# Revit family: Furniture_Table_Spacestor_Circa Boardroom Table
name_source: partatom
category: Furniture
revit_build: Autodesk Revit 2017 (Build: 20160225_1515(x64)
units: mm (PartAtom-declared; Revit-internal decimal feet)

## family parameters
Always vertical = Yes
Cut with Voids When Loaded = No
OmniClass Number = 23.40.20.00
OmniClass Title = General Furniture and Specialties
Room Calculation Point = No
Shared = No
Work Plane-Based = No

## types (23) — shared parameters
Assembly Code = E2020200
Fabric Finish = <By Category>
Legs Finish = <By Category>
Manufacturer = Spacestor
Table Top Finish = Spacestor White
URL = http://spacestor.uk.com

## per-type parameters (varying)
| type | Boat | Circular | Depth | Double D End | Oval | Rectangular | Width |
| boat-shaped - 2000w x 1000_800d x 727h | Yes | No | 1000 mm  [stored 3.28084 ft] | No | No | No | 2000 mm  [stored 6.56168 ft] |
| oval-shaped - 2000w x 1000d x 727h | No | No | 1000 mm  [stored 3.28084 ft] | No | Yes | No | 2000 mm  [stored 6.56168 ft] |
| double d-ended - 2000w x 1000d x 727h | No | No | 1000 mm  [stored 3.28084 ft] | Yes | No | No | 2000 mm  [stored 6.56168 ft] |
| circular - 1000 DIA x 727h | No | Yes | 1000 mm  [stored 3.28084 ft] | No | No | No | 3000 mm  [stored 9.84252 ft] |
| boat-shaped - 2400w x 1200_1000d x 727h | Yes | No | 1000 mm  [stored 3.28084 ft] | No | No | No | 2400 mm  [stored 7.87402 ft] |
| boat-shaped - 3000w x 1200_1000d x 727h | Yes | No | 1200 mm | No | No | No | 3000 mm  [stored 9.84252 ft] |
| boat-shaped - 3600w x 1200_1000d x 727h | Yes | No | 1200 mm | No | No | No | 3600 mm  [stored 11.811 ft] |
| boat-shaped - 4800w x 1200_1000d x 727h | Yes | No | 1200 mm | No | No | No | 4800 mm |
| circular - 1200 DIA x 727h | No | Yes | 1200 mm | No | No | No | 3000 mm  [stored 9.84252 ft] |
| circular - 800 DIA x 727h | No | Yes | 800 mm  [stored 2.62467 ft] | No | No | No | 3000 mm  [stored 9.84252 ft] |
| double d-ended - 2400w x 1200d x 727h | No | No | 1200 mm | Yes | No | No | 2400 mm  [stored 7.87402 ft] |
| double d-ended - 3000w x 1200d x 727h | No | No | 1200 mm | Yes | No | No | 3000 mm  [stored 9.84252 ft] |
| double d-ended - 3600w x 1200d x 727h | No | No | 1200 mm | Yes | No | No | 3600 mm  [stored 11.811 ft] |
| double d-ended - 4800w x 1200d x 727h | No | No | 1200 mm | Yes | No | No | 4800 mm |
| oval-shaped - 2400w x 1200d x 727h | No | No | 1200 mm | No | Yes | No | 2400 mm  [stored 7.87402 ft] |
| oval-shaped - 3000w x 1200d x 727h | No | No | 1200 mm | No | Yes | No | 3000 mm  [stored 9.84252 ft] |
| oval-shaped - 3600w x 1200d x 727h | No | No | 1200 mm | No | Yes | No | 3600 mm  [stored 11.811 ft] |
| rectangular - 1800w x 800d x 727h | No | No | 800 mm  [stored 2.62467 ft] | No | No | Yes | 1800 mm  [stored 5.90551 ft] |
| rectangular - 2000w x 1000d x 727h | No | No | 1000 mm  [stored 3.28084 ft] | No | No | Yes | 2000 mm  [stored 6.56168 ft] |
| rectangular - 2400w x 1200d x 727h | No | No | 1200 mm | No | No | Yes | 2400 mm  [stored 7.87402 ft] |
| rectangular - 3000w x 1200d x 727h | No | No | 1200 mm | No | No | Yes | 3000 mm  [stored 9.84252 ft] |
| rectangular - 3600w x 1200d x 727h | No | No | 1200 mm | No | No | Yes | 3600 mm  [stored 11.811 ft] |
| rectangular - 4800w x 1200d x 727h | No | No | 1200 mm | No | No | Yes | 4800 mm |

note: [stored X ft] marks values corroborated as IEEE doubles in the binary element streams (Revit-internal decimal feet)

## geometry (parser evidence)
native form markers: Sweep x20
no freeform markers — native parametric forms only
